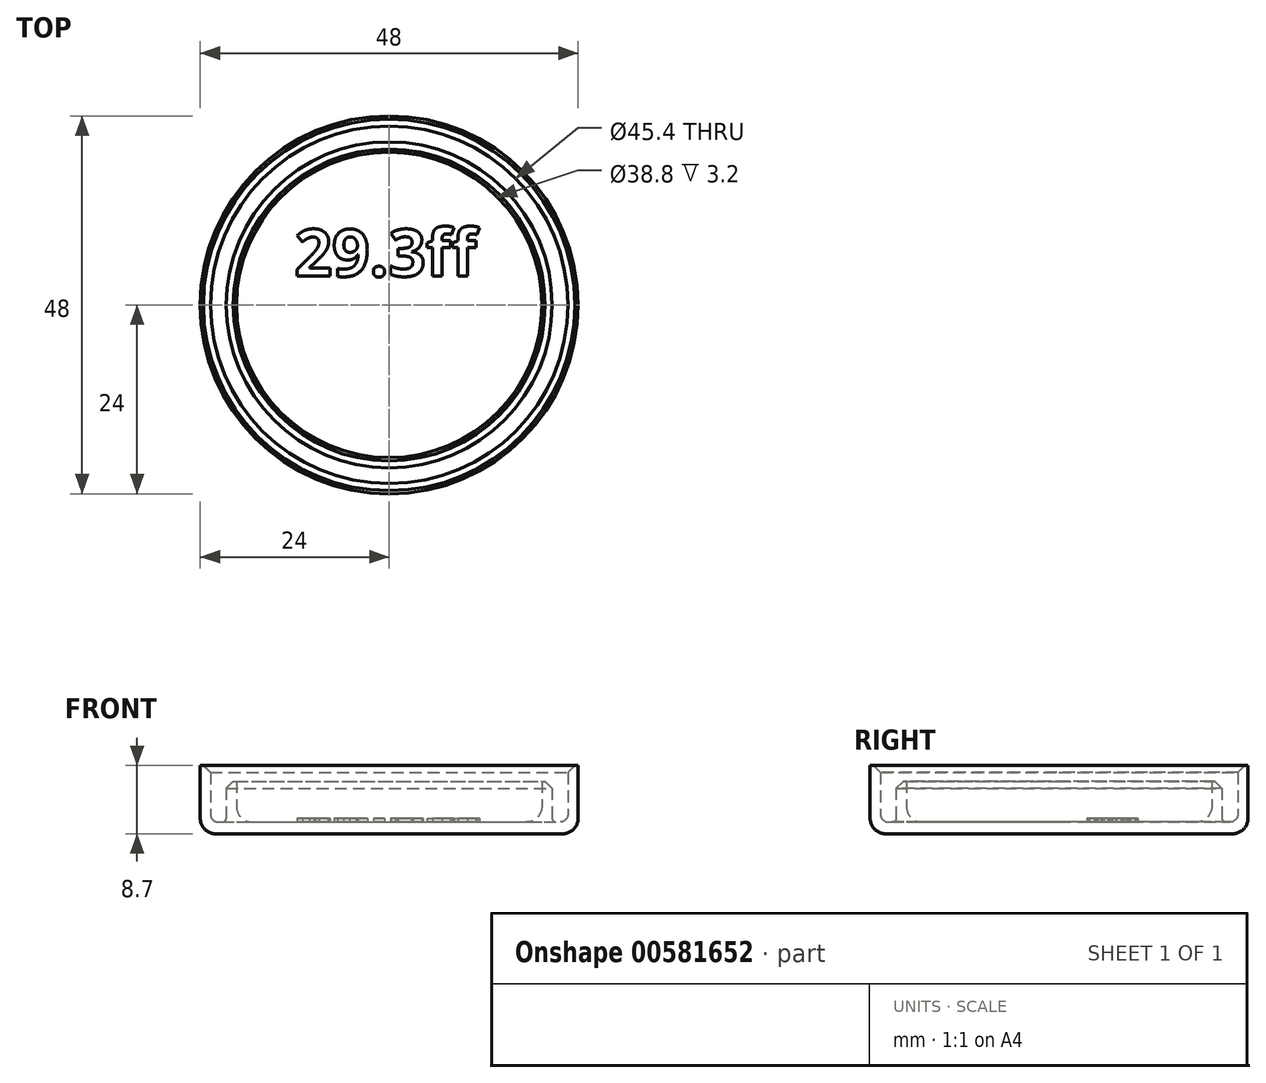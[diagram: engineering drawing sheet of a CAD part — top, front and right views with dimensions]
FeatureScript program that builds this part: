
annotation { "Feature Type Name" : "Feature", "Feature Type Description" : "" }
export const myFeature = defineFeature(function(context is Context, id is Id, definition is map)
    precondition{}
    {
        {
            var Q0;
            Q0=qCreatedBy(makeId("Front.planeOp"),FACE);
            var sketch = newSketch(context, id + "F0", { "sketchPlane" : qUnion([Q0])});
            skLineSegment(sketch, "E0", {"start": v(0, 0) * mm, "end": v(22, 0) * mm});
            skLineSegment(sketch, "E1", {"start": v(0, 0) * mm, "end": v(0, 1.5) * mm});
            skLineSegment(sketch, "E2", {"start": v(0, 1.5) * mm, "end": v(17.4, 1.5) * mm});
            skLineSegment(sketch, "E3", {"start": v(19.4, 3.5) * mm, "end": v(19.4, 6.7) * mm});
            skLineSegment(sketch, "E4", {"start": v(19.4, 6.7) * mm, "end": v(19.8, 6.7) * mm});
            skLineSegment(sketch, "E5", {"start": v(19.8, 6.7) * mm, "end": v(20.7, 5.8) * mm});
            skLineSegment(sketch, "E6", {"start": v(20.7, 5.8) * mm, "end": v(20.7, 2) * mm});
            skLineSegment(sketch, "E7", {"start": v(21.2, 1.5) * mm, "end": v(21.7, 1.5) * mm});
            skLineSegment(sketch, "E8", {"start": v(22.7, 2.5) * mm, "end": v(22.7, 7.8) * mm});
            skLineSegment(sketch, "E9", {"start": v(22.7, 7.8) * mm, "end": v(23.6, 8.7) * mm});
            skLineSegment(sketch, "E10", {"start": v(23.6, 8.7) * mm, "end": v(24, 8.7) * mm});
            skLineSegment(sketch, "E11", {"start": v(24, 8.7) * mm, "end": v(24, 2) * mm});
            skArc(sketch, "E12", {"start": v(17.4, 1.5) * mm, "mid": v(18.81, 2.09) * mm, "end": v(19.4, 3.5) * mm});
            skArc(sketch, "E13", {"start": v(22, 0) * mm, "mid": v(23.41, 0.59) * mm, "end": v(24, 2) * mm});
            skPoint(sketch, "E14.visualSharp", {"position": v(22.7, 1.5) * mm});
            skArc(sketch, "E14.filletArc", {"start": v(21.7, 1.5) * mm, "mid": v(22.4, 1.8) * mm, "end": v(22.7, 2.5) * mm});
            skPoint(sketch, "E15.visualSharp", {"position": v(20.7, 1.5) * mm});
            skArc(sketch, "E15.filletArc", {"start": v(20.7, 2) * mm, "mid": v(20.85, 1.65) * mm, "end": v(21.2, 1.5) * mm});
            skSolve(sketch);
        }
        {
            var Q0;
            Q0=qSketchRegion(id+"F0",true);
            var Q1;
            Q1=sQuery(id+"F0.wireOp",EDGE,"E1");
            revolve(context, id + "F1", {"entities" : qUnion([Q0]), "axis" : qUnion([Q1]), "revolveType" : RevolveType.FULL});
        }
        {
            var Q0;
            Q0=makeQuery(id+"F1.opRevolve","SWEPT_FACE",FACE,{"disambiguationData":[OSD([sQuery(id+"F0.wireOp",EDGE,"E2")])]});
            var sketch = newSketch(context, id + "F2", { "sketchPlane" : qUnion([Q0])});
            skText(sketch, "E16", { "text": "29.3ff", "fontName": "OpenSans-Bold.ttf"});
            const initialGuessF2  = {"E16": [-0.012, 0.00364, 1, 0, 0.006]};
            skSetInitialGuess(sketch, initialGuessF2);
            skSolve(sketch);
        }
        {
            var Q0;
            Q0=qSketchRegion(id+"F2",true);
            extrude(context, id + "F3", {"entities" : qUnion([Q0]), "operationType" : NewBodyOperationType.ADD, "depth" : 0.5 * mm});
        }
    });
